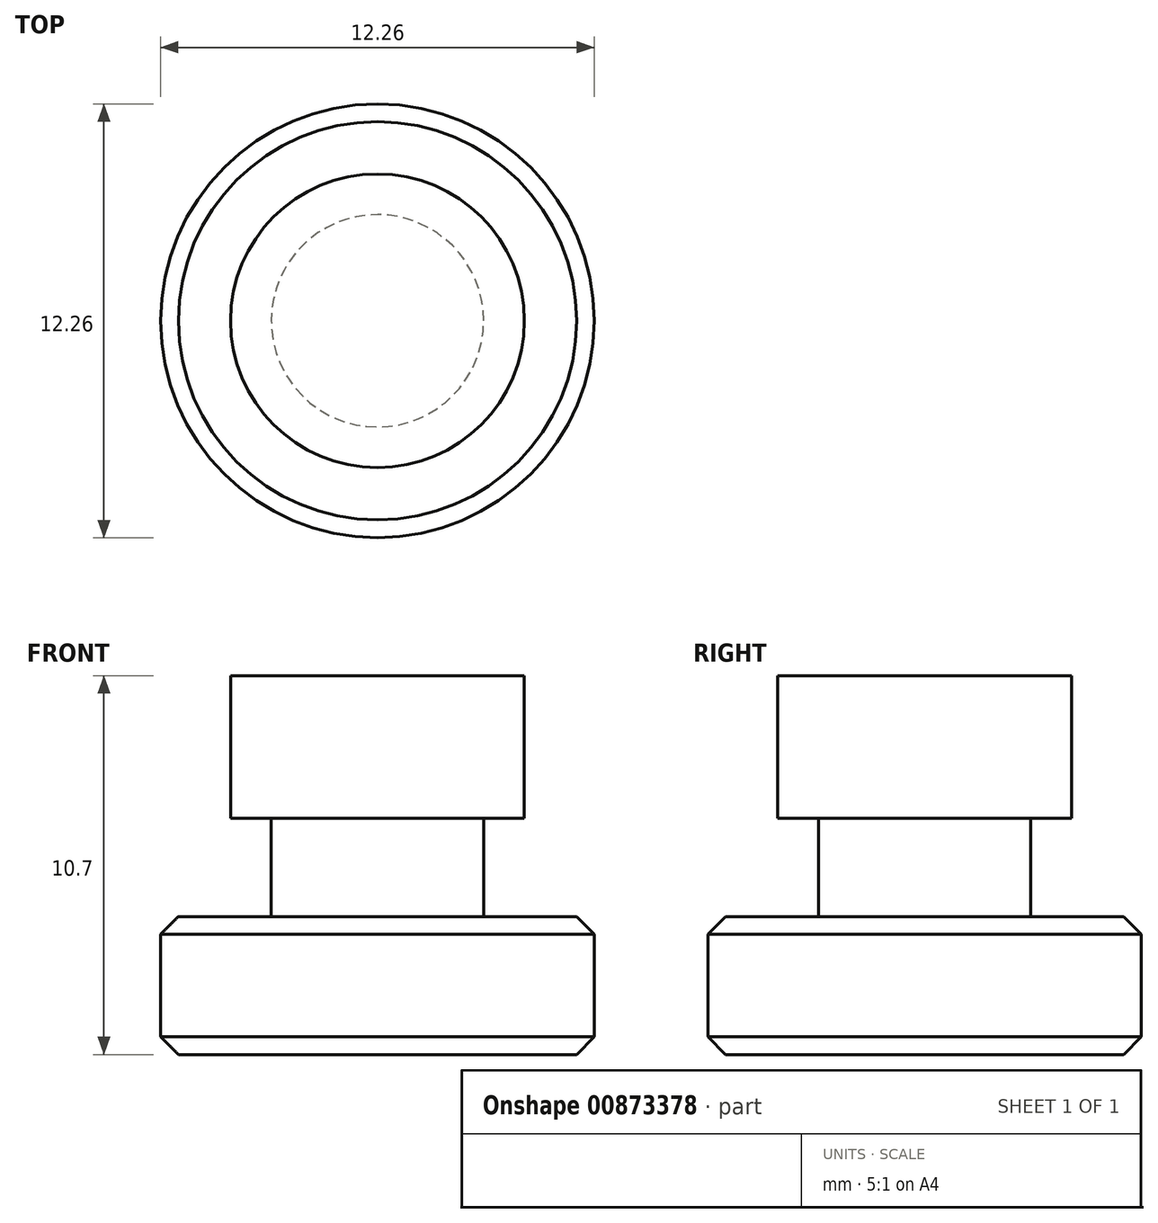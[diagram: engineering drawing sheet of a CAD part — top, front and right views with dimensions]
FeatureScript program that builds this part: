
annotation { "Feature Type Name" : "Feature", "Feature Type Description" : "" }
export const myFeature = defineFeature(function(context is Context, id is Id, definition is map)
    precondition{}
    {
        {
            var Q0;
            Q0=qCreatedBy(makeId("Top.planeOp"),FACE);
            var sketch = newSketch(context, id + "F0", { "sketchPlane" : qUnion([Q0])});
            skCircle(sketch, "E0", {"center": v(0, 0) * mm, "radius": 3 * mm});
            skSolve(sketch);
        }
        {
            var Q0;
            Q0 = qSketchRegion(id + "F0", true);
            extrude(context, id + "F1", {"entities" : qUnion([Q0]), "depth" : 6.8 * mm, "offsetDistance" : 25 * mm});
        }
        {
            var Q0;
            Q0=makeQuery(id+"F1.opExtrude","CAP_FACE",FACE,{"disambiguationData":[OSD([sQuery(id+"F0.wireOp",EDGE,"E0")])],"isStart":true});
            var sketch = newSketch(context, id + "F2", { "sketchPlane" : qUnion([Q0])});
            skCircle(sketch, "E1", {"center": v(0, 0) * mm, "radius": 6.12 * mm});
            skSolve(sketch);
        }
        {
            var Q0;
            Q0 = qSketchRegion(id + "F2", true);
            extrude(context, id + "F3", {"entities" : qUnion([Q0]), "operationType" : NewBodyOperationType.ADD, "depth" : 3.9 * mm, "offsetDistance" : 25 * mm});
        }
        {
            var Q0;
            Q0=makeQuery(id+"F3.opExtrude","CAP_EDGE",EDGE,{"disambiguationData":[OSD([sQuery(id+"F2.wireOp",EDGE,"E1")])],"isStart":true});
            var Q1;
            Q1=makeQuery(id+"F3.opExtrude","CAP_EDGE",EDGE,{"disambiguationData":[OSD([sQuery(id+"F2.wireOp",EDGE,"E1")])],"isStart":false});
            chamfer(context, id + "F4", {"entities" : qUnion([Q0, Q1]), "width" : .5 * mm, "tangentPropagation" : true});
        }
        {
            var Q0;
            Q0=makeQuery(id+"F1.opExtrude","CAP_FACE",FACE,{"disambiguationData":[OSD([sQuery(id+"F0.wireOp",EDGE,"E0")])],"isStart":false});
            var sketch = newSketch(context, id + "F5", { "sketchPlane" : qUnion([Q0])});
            skCircle(sketch, "E2", {"center": v(0, 0) * mm, "radius": 4.15 * mm});
            skSolve(sketch);
        }
        {
            var Q0;
            Q0 = qSketchRegion(id + "F5", true);
            extrude(context, id + "F6", {"entities" : qUnion([Q0]), "operationType" : NewBodyOperationType.ADD, "oppositeDirection" : true, "depth" : 4.02 * mm, "offsetDistance" : 25 * mm});
        }
    });
